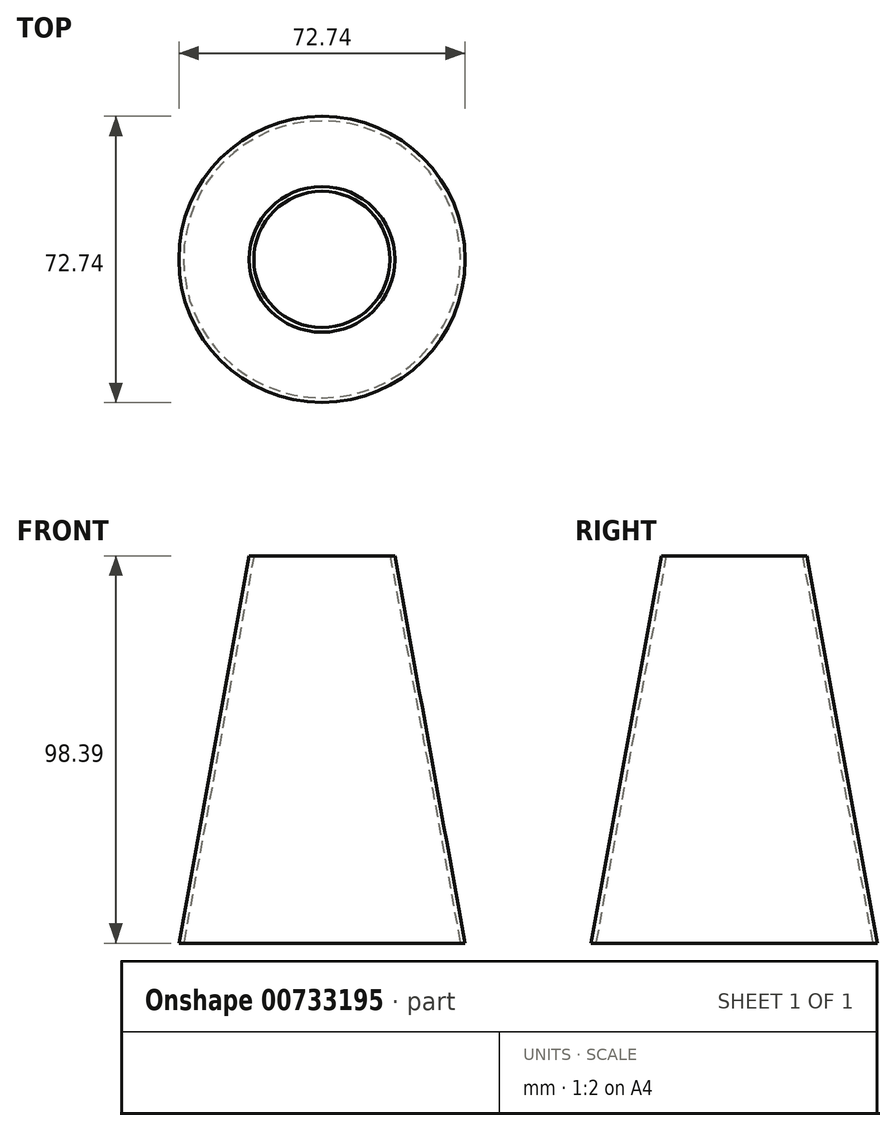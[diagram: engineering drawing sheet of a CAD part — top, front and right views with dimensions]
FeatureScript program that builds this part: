
annotation { "Feature Type Name" : "Feature", "Feature Type Description" : "" }
export const myFeature = defineFeature(function(context is Context, id is Id, definition is map)
    precondition{}
    {
        {
            var Q0;
            Q0=qCreatedBy(makeId("Right.planeOp"),FACE);
            var sketch = newSketch(context, id + "F0", { "sketchPlane" : qUnion([Q0])});
            skLineSegment(sketch, "E0", {"start": v(0, 0) * mm, "end": v(17.87, -98.4) * mm});
            skLineSegment(sketch, "E1", {"start": v(17.87, -98.4) * mm, "end": v(16.67, -98.4) * mm});
            skLineSegment(sketch, "E2", {"start": v(-18.5, 0) * mm, "end": v(-18.5, -96.38) * mm, "construction": true});
            skLineSegment(sketch, "E3", {"start": v(16.67, -98.4) * mm, "end": v(-1.2, 0) * mm});
            skLineSegment(sketch, "E4", {"start": v(-1.2, 0) * mm, "end": v(0, 0) * mm});
            skSolve(sketch);
        }
        {
            var Q0;
            Q0=makeQuery(id+"F0.imprint","IMPRINT",FACE,{"disambiguationData":[TD([[makeQuery(id+"F0.imprint","IMPRINT",EDGE,{"derivedFrom":sQuery(id+"F0.wireOp",EDGE,"E0")}),-1.0]])]});
            var Q1;
            Q1=sQuery(id+"F0.wireOp",EDGE,"E2");
            revolve(context, id + "F1", {"surfaceOperationType" : NewSurfaceOperationType.NEW, "entities" : qUnion([Q0]), "axis" : qUnion([Q1]), "revolveType" : RevolveType.FULL});
        }
    });
